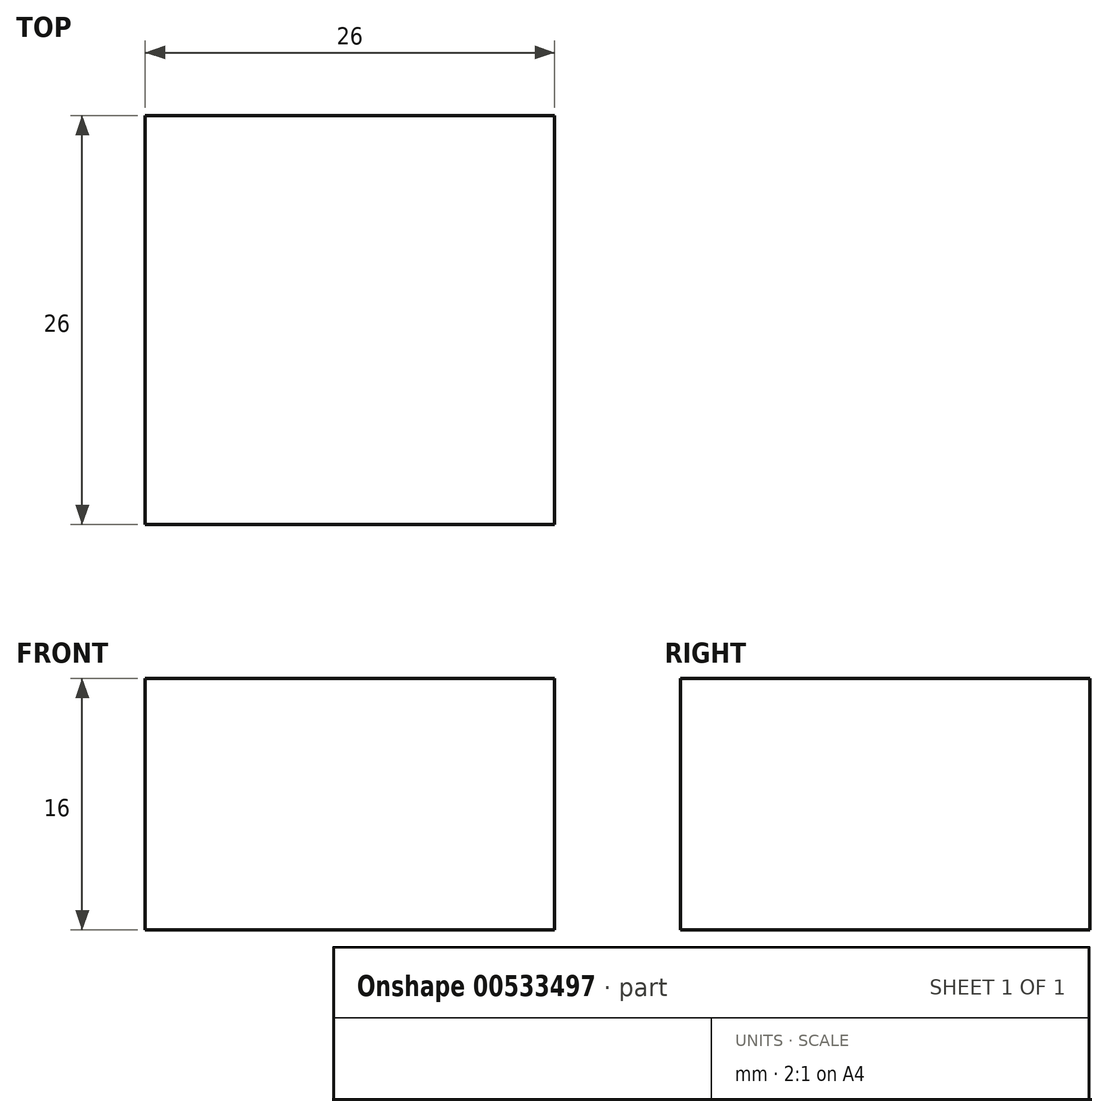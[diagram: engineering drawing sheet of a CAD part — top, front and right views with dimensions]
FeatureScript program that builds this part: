
annotation { "Feature Type Name" : "Feature", "Feature Type Description" : "" }
export const myFeature = defineFeature(function(context is Context, id is Id, definition is map)
    precondition{}
    {
        {
            var Q0;
            Q0=qCreatedBy(makeId("Top.planeOp"),FACE);
            var sketch = newSketch(context, id + "F0", { "sketchPlane" : qUnion([Q0])});
            skLineSegment(sketch, "E0.bottom", {"start": v(0, 0) * mm, "end": v(26, 0) * mm});
            skLineSegment(sketch, "E0.top", {"start": v(0, 26) * mm, "end": v(26, 26) * mm});
            skLineSegment(sketch, "E0.left", {"start": v(0, 0) * mm, "end": v(0, 26) * mm});
            skLineSegment(sketch, "E0.right", {"start": v(26, 0) * mm, "end": v(26, 26) * mm});
            skSolve(sketch);
        }
        {
            var Q0;
            Q0=qSketchRegion(id+"F0",true);
            extrude(context, id + "F1", {"entities" : qUnion([Q0]), "depth" : 16 * mm, "offsetDistance" : 25 * mm});
        }
    });
